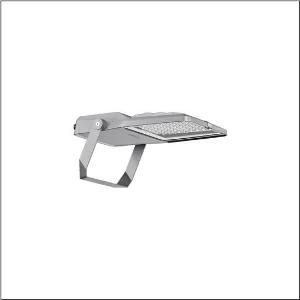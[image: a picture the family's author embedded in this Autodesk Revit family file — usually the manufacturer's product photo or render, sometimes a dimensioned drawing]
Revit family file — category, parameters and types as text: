
# Revit family: floodlight_fl_21_mini___pl43_5xa7775d2a1a_a4ba
name_source: partatom
category: Lighting Fixtures
units: mm (PartAtom-declared; Revit-internal decimal feet)

## family parameters
Cut with Voids When Loaded = No
Host = Face
Light Source = No
Part Type = Normal
Room Calculation Point = No
Round Connector Dimension = Use Diameter
Shared = No

## types (1)
- --- (1 x LED, 18300 lm, 142.9 W, 3000K)
    Apparent Load = 143 VA
    CIE Flux Codes = 27 78 99 100 100
    Color Rendering = 70
    Color Temperature = 3000K
    Default Elevation = 1800 mm
    Description = Floodlight FL 21 mini, floodlight, primary light control with lens, of PMMA, primary optical cover: protective disc, of toughened safety glass, transparent, light distribution: PL43, light emission: direct distribution, installation type: surface-mounted, LED, High Power LED, rated luminous flux: 18.300lm, luminous efficacy: 128lm/W, light colour: 730, colour temperature: 3000K, control: flexible luminous flux parameterisation, time-dependent luminous flux control, constant luminous flux control, overheat protection, presetting dimming logarithmic, with terminal, 6-pole, mains connection: 220..240V, AC, 50/60Hz, start of lifetime: 143W, end of service life: 151W, reduction: 63W, luminaire housing, of diecast aluminium, powder-coated, Siteco® metallic grey (DB 702S), corrosivity category C5 mid according to DIN EN ISO 12944, sealing non-destructively replaceable, mounting bracket, of steel, galvanised, powder-coated, Siteco® metallic grey (DB 702S), Smart Interface above, protection rating (complete): IP66, insulation class (complete): insulation class II (safety insulation), certification: CE, ENEC, VDE, protection symbol: D, impact resistance: IK08, permissible operating ambient temperature: -40..+40°C, permissible operating ambient temperature for outdoor applications: -40..+50°C, standard: DIN EN 12944, LABS conformity tested according to VDMA 24364:2018-05, packaging unit: 1 piece

Light Distribution: PL43
    Height = 70 mm
    Lamp = 1 x LED
    Lamp Light Flux = 18300 lm
    Lamp Power = 142.9 W
    Lamp count = 1
    Length = 485 mm
    Luminous efficacy = 128 lm/W
    Manufacturer = Siteco
    ModVariant = No
    Model = 5XA7775D2A1A
    Number of Poles = 1
    OnlyDefault = Yes
    Power Factor = 1
    Product Name = Floodlight FL 21 mini | PL43
    Product group = floodlight | pylon annexe
    ProductGroupID = 6200
    Protection Class = Protection class II
    Protection Degree = IP 66
    RLX_Detail_Level = 1
    RLX_Emergency_Light_Flux = 0 lm
    RLX_Emergency_Type = 0
    RLX_Emergency_Type_DB = No
    RlxData = <blob elided: 96105 chars, md5=121ed7ba>
    Socket = socket
    Standby Power = 0 W
    System Light Flux = 18300 lm
    System Power = 143 W
    Type Comments = factory setting: luminous flux: 100 % | dim-lin: 254 | 730 mA
    Type Image = l_1006845.jpg
    URL = http://relux.com
    VarID = @adj_111211
    Voltage = 0 V
    Weight = 0.00 kg
    Width = 337 mm

## geometry (parser evidence)
native form markers: Blend x4, Sweep x11
no freeform markers — native parametric forms only
